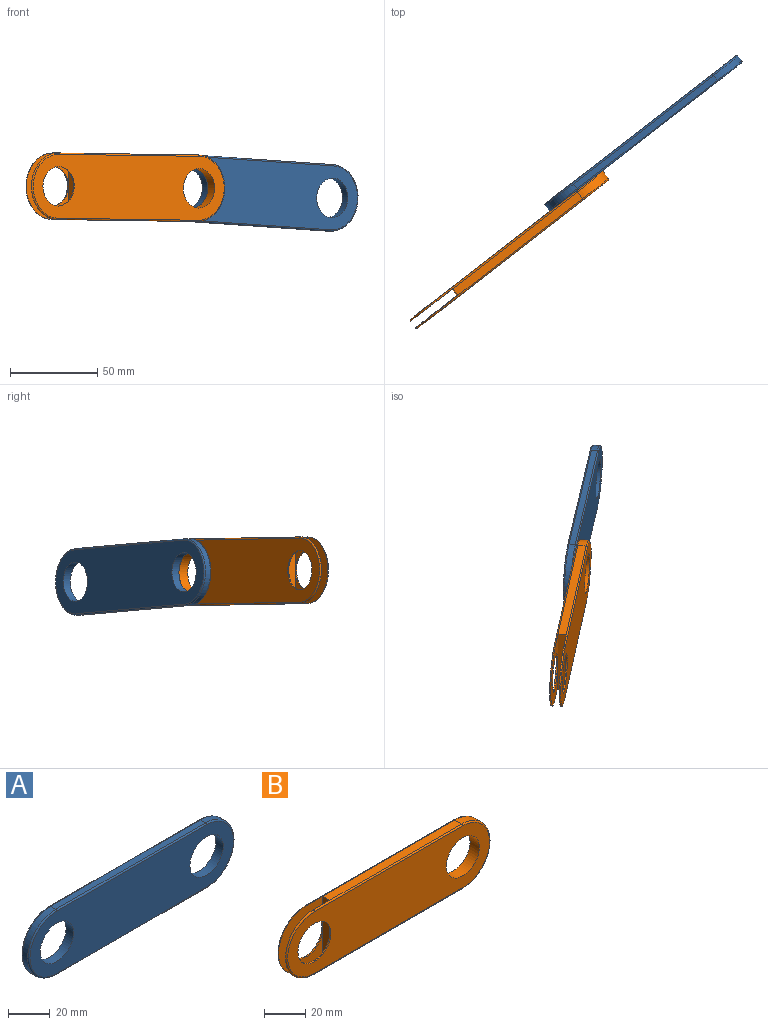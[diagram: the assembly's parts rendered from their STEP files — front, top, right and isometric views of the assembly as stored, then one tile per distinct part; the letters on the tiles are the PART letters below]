
ASSEMBLY  parts=2 mates=1
PART A: 16 faces, bbox 142.8x5.1x41.2 mm
  f0: plane 101.6x3.56mm, normal (0,0,1), area 361.3mm2, adj f1,f3,f6,f10
  f1: cylinder r=19.05mm len=38.1mm, axis (0,1,0), area 212.8mm2, adj f0,f2,f7,f11
  f2: plane 101.6x3.56mm, normal (0,0,-1), area 361.3mm2, adj f1,f3,f9,f13
  f3: cylinder r=19.05mm len=38.1mm, axis (0,1,0), area 212.8mm2, adj f0,f2,f8,f12
  f4: plane 138.18x36.58mm, normal (0,-1,0), area 3964.1mm2, adj f10,f11,f12,f13,f14,f15
  f5: plane 138.18x36.58mm, normal (0,1,0), area 3964.1mm2, adj f6,f7,f8,f9,f14,f15
  f6: cylinder r=0.76mm len=101.6mm, axis (-1,0,0), area 121.6mm2, adj f0,f5,f7,f8
  f7: torus R=18.29mm, axis (0,-1,0), area 70.6mm2, adj f1,f5,f6,f9
  f8: torus R=18.29mm, axis (0,-1,0), area 70.6mm2, adj f3,f5,f6,f9
  f9: cylinder r=0.76mm len=101.6mm, axis (1,0,0), area 121.6mm2, adj f2,f5,f7,f8
  f10: cylinder r=0.76mm len=101.6mm, axis (1,0,0), area 121.6mm2, adj f0,f4,f11,f12
  f11: torus R=18.29mm, axis (0,-1,0), area 70.6mm2, adj f1,f4,f10,f13
  f12: torus R=18.29mm, axis (0,-1,0), area 70.6mm2, adj f3,f4,f10,f13
  f13: cylinder r=0.76mm len=101.6mm, axis (-1,0,0), area 121.6mm2, adj f2,f4,f11,f12
  f14: cylinder r=11.3mm len=22.61mm, axis (0,-1,0), area 360.8mm2, adj f4,f5
  f15: cylinder r=11.3mm len=22.61mm, axis (0,-1,0), area 360.8mm2, adj f4,f5
PART B: 20 faces, bbox 142.8x6.4x41.2 mm
  f0: torus R=18.29mm, axis (0,-1,0), area 70.6mm2, adj f1,f7,f13,f19
  f1: cylinder r=0.76mm len=101.6mm, axis (-1,0,0), area 121.6mm2, adj f0,f5,f7,f14,f19
  f2: cylinder r=11.3mm len=22.61mm, axis (0,-1,0), area 54.1mm2, adj f7,f19
  f3: plane 101.6x4.83mm, normal (0,0,1), area 435.6mm2, adj f4,f6,f9,f13,f17,f18
  f4: cylinder r=19.05mm len=38.1mm, axis (0,1,0), area 0.4mm2, adj f3,f5,f10,f18
  f5: plane 101.6x4.83mm, normal (0,0,-1), area 435.6mm2, adj f1,f4,f6,f12,f17,f18
  f6: cylinder r=19.05mm len=38.1mm, axis (0,1,0), area 288.8mm2, adj f3,f5,f11,f14
  f7: plane 138.18x36.58mm, normal (0,-1,0), area 3964.1mm2, adj f0,f1,f2,f13,f14,f15
  f8: plane 138.18x36.58mm, normal (0,1,0), area 3964.1mm2, adj f9,f10,f11,f12,f15,f16
  f9: cylinder r=0.76mm len=101.6mm, axis (-1,0,0), area 121.6mm2, adj f3,f8,f10,f11
  f10: torus R=18.29mm, axis (0,-1,0), area 70.6mm2, adj f4,f8,f9,f12
  f11: torus R=18.29mm, axis (0,-1,0), area 70.6mm2, adj f6,f8,f9,f12
  f12: cylinder r=0.76mm len=101.6mm, axis (1,0,0), area 121.6mm2, adj f5,f8,f10,f11
  f13: cylinder r=0.76mm len=101.6mm, axis (1,0,0), area 121.6mm2, adj f0,f3,f7,f14,f19
  f14: torus R=18.29mm, axis (0,-1,0), area 70.6mm2, adj f1,f6,f7,f13
  f15: cylinder r=11.3mm len=22.61mm, axis (0,-1,0), area 451mm2, adj f7,f8
  f16: cylinder r=11.3mm len=22.61mm, axis (0,-1,0), area 54.6mm2, adj f8,f18
  f17: plane 38.1x4.82mm, normal (-1,0,0), area 183.6mm2, adj f3,f5,f18,f19
  f18: plane 38.1x30.41mm, normal (0,-1,0), area 601.4mm2, adj f3,f4,f5,f16,f17
  f19: plane 38.1x30.41mm, normal (0,1,0), area 601.4mm2, adj f0,f1,f2,f13,f17
PLACE A rot(axis=(0.32,-0.95,0),176.9deg) t=(-1.25,66.93,137.81)mm
PLACE B rot(axis=(0.01,0.02,1),37.8deg) t=(-77.22,0.8,140.74)mm
MATE revolute B.f6 <-> A.f3  axis (0.61,-0.79,-0.01) through (-35.51,29.11,140.3)mm
